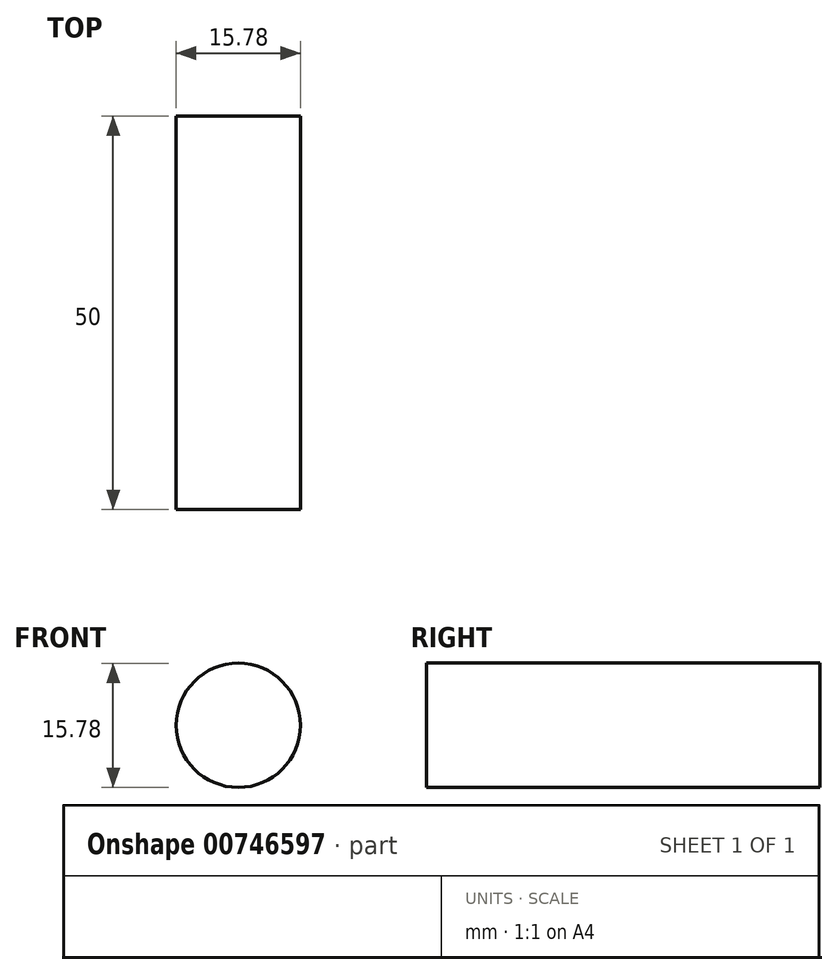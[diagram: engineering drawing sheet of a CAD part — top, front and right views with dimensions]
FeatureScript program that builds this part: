
annotation { "Feature Type Name" : "Feature", "Feature Type Description" : "" }
export const myFeature = defineFeature(function(context is Context, id is Id, definition is map)
    precondition{}
    {
        {
            var Q0;
            Q0=qCreatedBy(makeId("Front.planeOp"),FACE);
            var sketch = newSketch(context, id + "F0", { "sketchPlane" : qUnion([Q0])});
            skCircle(sketch, "E0", {"center": v(0, 0) * mm, "radius": 7.9 * mm});
            skSolve(sketch);
        }
        {
            var Q0;
            Q0 = qSketchRegion(id + "F0", true);
            extrude(context, id + "F1", {"entities" : qUnion([Q0]), "depth" : 50 * mm, "offsetDistance" : 25 * mm});
        }
    });
